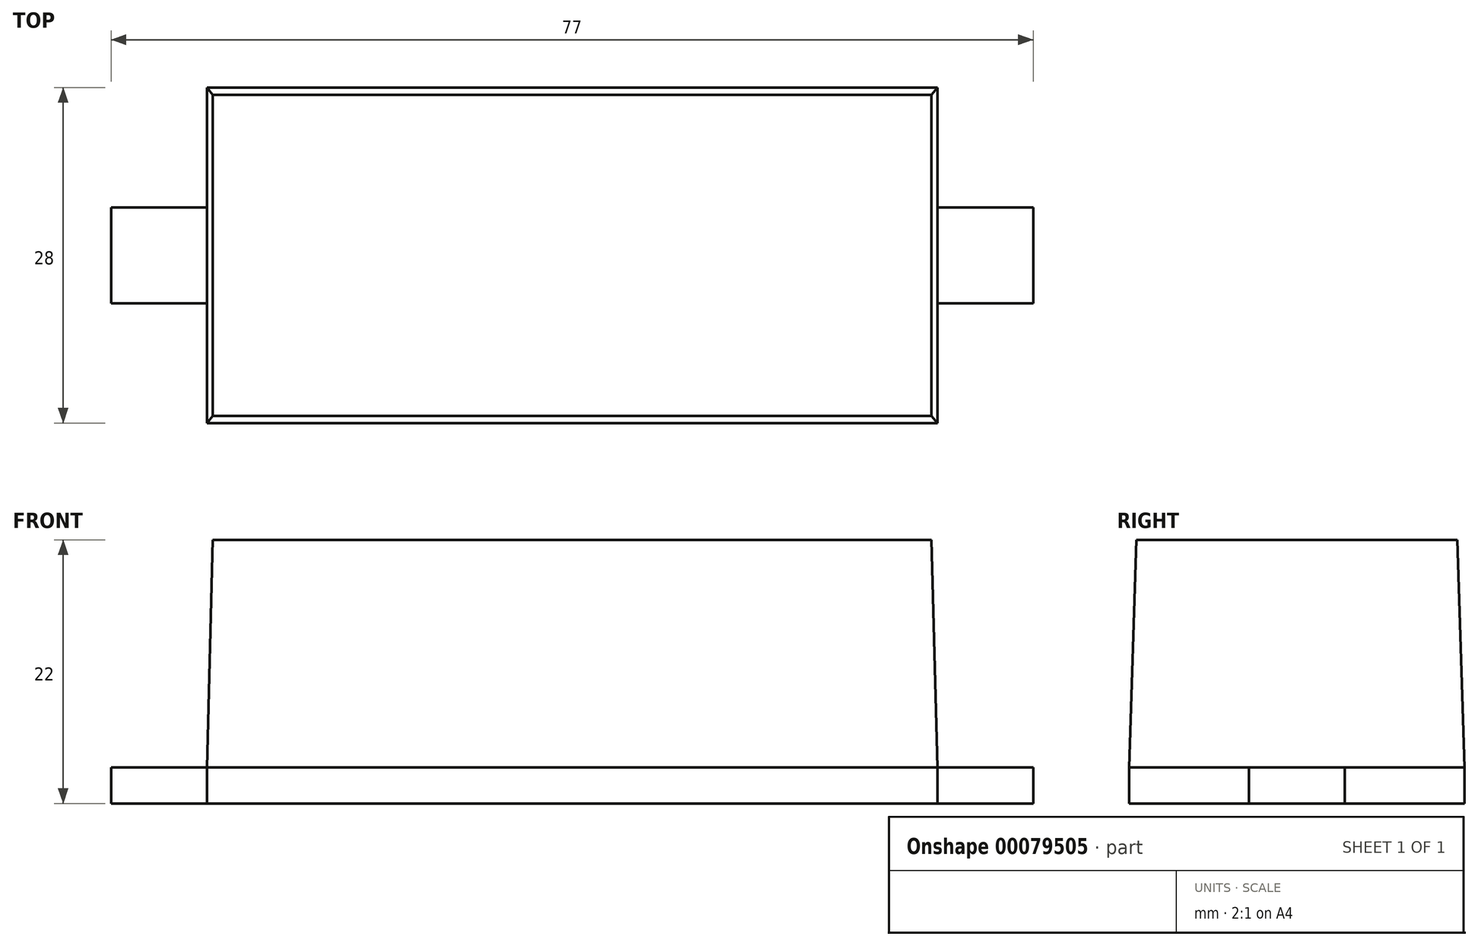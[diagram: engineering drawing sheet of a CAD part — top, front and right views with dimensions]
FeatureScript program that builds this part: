
annotation { "Feature Type Name" : "Feature", "Feature Type Description" : "" }
export const myFeature = defineFeature(function(context is Context, id is Id, definition is map)
    precondition{}
    {
        {
            var Q0;
            Q0=qCreatedBy(makeId("Front.planeOp"),FACE);
            var sketch = newSketch(context, id + "F0", { "sketchPlane" : qUnion([Q0])});
            skLineSegment(sketch, "E0.bottom", {"start": v(-30, 22) * mm, "end": v(30, 22) * mm});
            skLineSegment(sketch, "E0.top", {"start": v(-30.5, 0) * mm, "end": v(30.5, 0) * mm});
            skLineSegment(sketch, "E0.left", {"start": v(-30, 22) * mm, "end": v(-30.5, 3) * mm});
            skLineSegment(sketch, "E0.right", {"start": v(30, 22) * mm, "end": v(30.5, 3) * mm});
            skLineSegment(sketch, "E1", {"start": v(30.5, 3) * mm, "end": v(30.5, 0) * mm});
            skLineSegment(sketch, "E2", {"start": v(-30.5, 3) * mm, "end": v(-30.5, 0) * mm});
            skSolve(sketch);
        }
        {
            var Q0;
            Q0 = qSketchRegion(id + "F0", true);
            extrude(context, id + "F1", {"entities" : qUnion([Q0]), "depth" : 30 * mm, "symmetric" : true});
        }
        {
            var Q0;
            Q0=qCreatedBy(makeId("Right.planeOp"),FACE);
            var sketch = newSketch(context, id + "F2", { "sketchPlane" : qUnion([Q0])});
            skLineSegment(sketch, "E3", {"start": v(-14, 0) * mm, "end": v(14, 0) * mm});
            skLineSegment(sketch, "E4", {"start": v(14, 3) * mm, "end": v(13.4, 22) * mm});
            skLineSegment(sketch, "E5", {"start": v(13.4, 22) * mm, "end": v(-13.4, 22) * mm});
            skLineSegment(sketch, "E6", {"start": v(-13.4, 22) * mm, "end": v(-14, 3) * mm});
            skLineSegment(sketch, "E7", {"start": v(14, 3) * mm, "end": v(14, 0) * mm});
            skLineSegment(sketch, "E8", {"start": v(-14, 3) * mm, "end": v(-14, 0) * mm});
            skLineSegment(sketch, "E9.0", {"start": v(-15, 3) * mm, "end": v(15, 3) * mm, "construction": true});
            skSolve(sketch);
        }
        {
            var Q0;
            Q0 = qSketchRegion(id + "F2", true);
            extrude(context, id + "F3", {"entities" : qUnion([Q0]), "operationType" : NewBodyOperationType.INTERSECT, "depth" : 70 * mm, "symmetric" : true});
        }
        {
            var Q0;
            Q0=makeQuery(id+"F1.opExtrude","SWEPT_FACE",FACE,{"disambiguationData":[OSD([sQuery(id+"F0.wireOp",EDGE,"E0.top")])]});
            var sketch = newSketch(context, id + "F4", { "sketchPlane" : qUnion([Q0])});
            skLineSegment(sketch, "E10.bottom", {"start": v(30.5, 4) * mm, "end": v(38.5, 4) * mm});
            skLineSegment(sketch, "E10.top", {"start": v(30.5, -4) * mm, "end": v(38.5, -4) * mm});
            skLineSegment(sketch, "E10.left", {"start": v(30.5, 4) * mm, "end": v(30.5, -4) * mm});
            skLineSegment(sketch, "E10.right", {"start": v(38.5, 4) * mm, "end": v(38.5, -4) * mm});
            skLineSegment(sketch, "E11", {"start": v(30.5, -4) * mm, "end": v(38.5, 4) * mm, "construction": true});
            skCircle(sketch, "E12", {"center": v(34.5, 0) * mm, "radius": 1.5 * mm, "construction": true});
            skSolve(sketch);
        }
        {
            var Q0;
            Q0 = qSketchRegion(id + "F4", true);
            extrude(context, id + "F5", {"entities" : qUnion([Q0]), "oppositeDirection" : true, "depth" : 3 * mm});
        }
        {
            var Q0;
            Q0=makeQuery(id+"F5.opExtrude","SWEPT_BODY",BODY,{"disambiguationData":[OSD([sQuery(id+"F4.wireOp",EDGE,"E10.bottom"),sQuery(id+"F4.wireOp",EDGE,"E10.top"),sQuery(id+"F4.wireOp",EDGE,"E10.left"),sQuery(id+"F4.wireOp",EDGE,"E10.right"),sQuery(id+"F4.wireOp",EDGE,"E12")])]});
            var Q1;
            Q1=qCreatedBy(makeId("Right.planeOp"),FACE);
            mirror(context, id + "F6", {"operationType" : NewBodyOperationType.ADD, "entities" : qUnion([Q0]), "mirrorPlane" : qUnion([Q1])});
        }
    });
